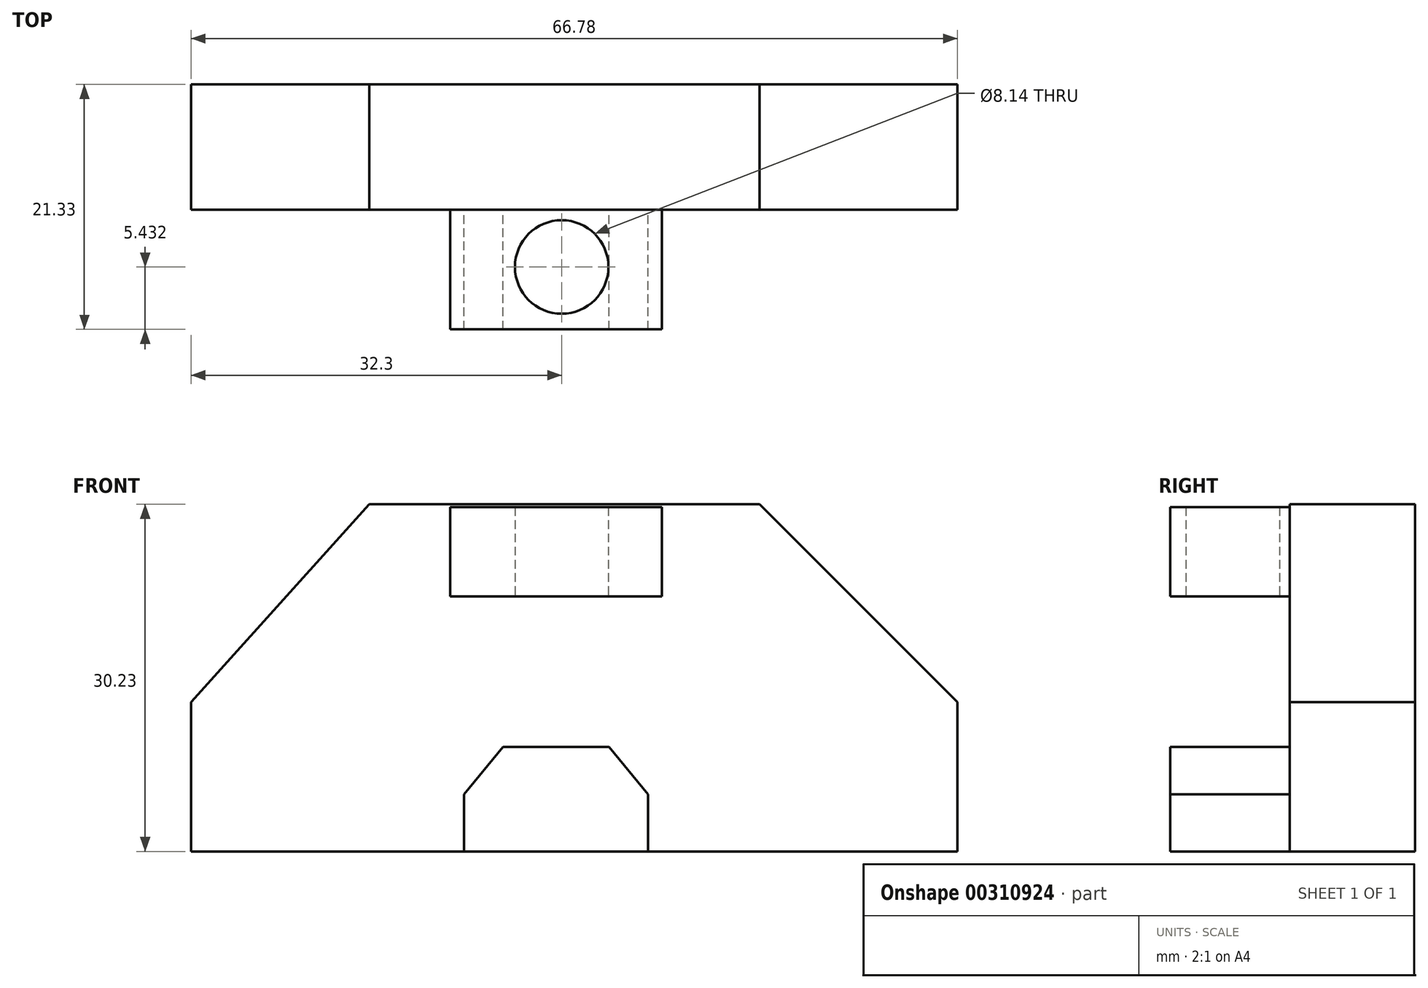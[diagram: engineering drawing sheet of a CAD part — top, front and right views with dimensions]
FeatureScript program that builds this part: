
annotation { "Feature Type Name" : "Feature", "Feature Type Description" : "" }
export const myFeature = defineFeature(function(context is Context, id is Id, definition is map)
    precondition{}
    {
        {
            var Q0;
            Q0=qCreatedBy(makeId("Front.planeOp"),FACE);
            var sketch = newSketch(context, id + "F0", { "sketchPlane" : qUnion([Q0])});
            skLineSegment(sketch, "E0.bottom", {"start": v(-30.6, 0) * mm, "end": v(36.18, 0) * mm});
            skLineSegment(sketch, "E0.top", {"start": v(-30.6, 13) * mm, "end": v(36.18, 13) * mm});
            skLineSegment(sketch, "E0.left", {"start": v(-30.6, 0) * mm, "end": v(-30.6, 13) * mm});
            skLineSegment(sketch, "E0.right", {"start": v(36.18, 0) * mm, "end": v(36.18, 13) * mm});
            skLineSegment(sketch, "E1", {"start": v(-30.6, 13) * mm, "end": v(-15.05, 30.23) * mm});
            skLineSegment(sketch, "E2", {"start": v(-15.05, 30.23) * mm, "end": v(18.94, 30.23) * mm});
            skLineSegment(sketch, "E3", {"start": v(18.94, 30.23) * mm, "end": v(36.18, 13) * mm});
            skSolve(sketch);
        }
        {
            var Q0;
            Q0 = qSketchRegion(id + "F0", true);
            extrude(context, id + "F1", {"entities" : qUnion([Q0]), "oppositeDirection" : true, "depth" : 10.92 * mm});
        }
        {
            var Q0;
            Q0=qCreatedBy(makeId("Front.planeOp"),FACE);
            var sketch = newSketch(context, id + "F2", { "sketchPlane" : qUnion([Q0])});
            skLineSegment(sketch, "E4.bottom", {"start": v(-8.01, 29.99) * mm, "end": v(10.44, 29.99) * mm});
            skLineSegment(sketch, "E4.top", {"start": v(-8.01, 22.22) * mm, "end": v(10.44, 22.22) * mm});
            skLineSegment(sketch, "E4.left", {"start": v(-8.01, 29.99) * mm, "end": v(-8.01, 22.22) * mm});
            skLineSegment(sketch, "E4.right", {"start": v(10.44, 29.99) * mm, "end": v(10.44, 22.22) * mm});
            skSolve(sketch);
        }
        {
            var Q0;
            Q0 = qSketchRegion(id + "F2", true);
            extrude(context, id + "F3", {"entities" : qUnion([Q0]), "operationType" : NewBodyOperationType.ADD, "depth" : 10.4 * mm});
        }
        {
            var Q0;
            Q0=qCreatedBy(makeId("Top.planeOp"),FACE);
            var sketch = newSketch(context, id + "F4", { "sketchPlane" : qUnion([Q0])});
            skCircle(sketch, "E5", {"center": v(1.7, -4.98) * mm, "radius": 4.07 * mm});
            skSolve(sketch);
        }
        {
            var Q0;
            Q0 = qSketchRegion(id + "F4", true);
            extrude(context, id + "F5", {"entities" : qUnion([Q0]), "operationType" : NewBodyOperationType.REMOVE, "depth" : 37.85 * mm});
        }
        {
            var Q0;
            Q0=qCreatedBy(makeId("Front.planeOp"),FACE);
            var sketch = newSketch(context, id + "F6", { "sketchPlane" : qUnion([Q0])});
            skLineSegment(sketch, "E6.bottom", {"start": v(-6.8, 0) * mm, "end": v(9.23, 0) * mm});
            skLineSegment(sketch, "E6.top", {"start": v(-6.8, 4.98) * mm, "end": v(9.23, 4.98) * mm});
            skLineSegment(sketch, "E6.left", {"start": v(-6.8, 0) * mm, "end": v(-6.8, 4.98) * mm});
            skLineSegment(sketch, "E6.right", {"start": v(9.23, 0) * mm, "end": v(9.23, 4.98) * mm});
            skLineSegment(sketch, "E7", {"start": v(-6.8, 4.98) * mm, "end": v(-3.4, 9.1) * mm});
            skLineSegment(sketch, "E8", {"start": v(9.23, 4.98) * mm, "end": v(5.83, 9.1) * mm});
            skLineSegment(sketch, "E9", {"start": v(5.83, 9.1) * mm, "end": v(-3.4, 9.1) * mm});
            skSolve(sketch);
        }
        {
            var Q0;
            Q0 = qSketchRegion(id + "F6", true);
            extrude(context, id + "F7", {"entities" : qUnion([Q0]), "operationType" : NewBodyOperationType.ADD, "depth" : 10.4 * mm});
        }
    });
